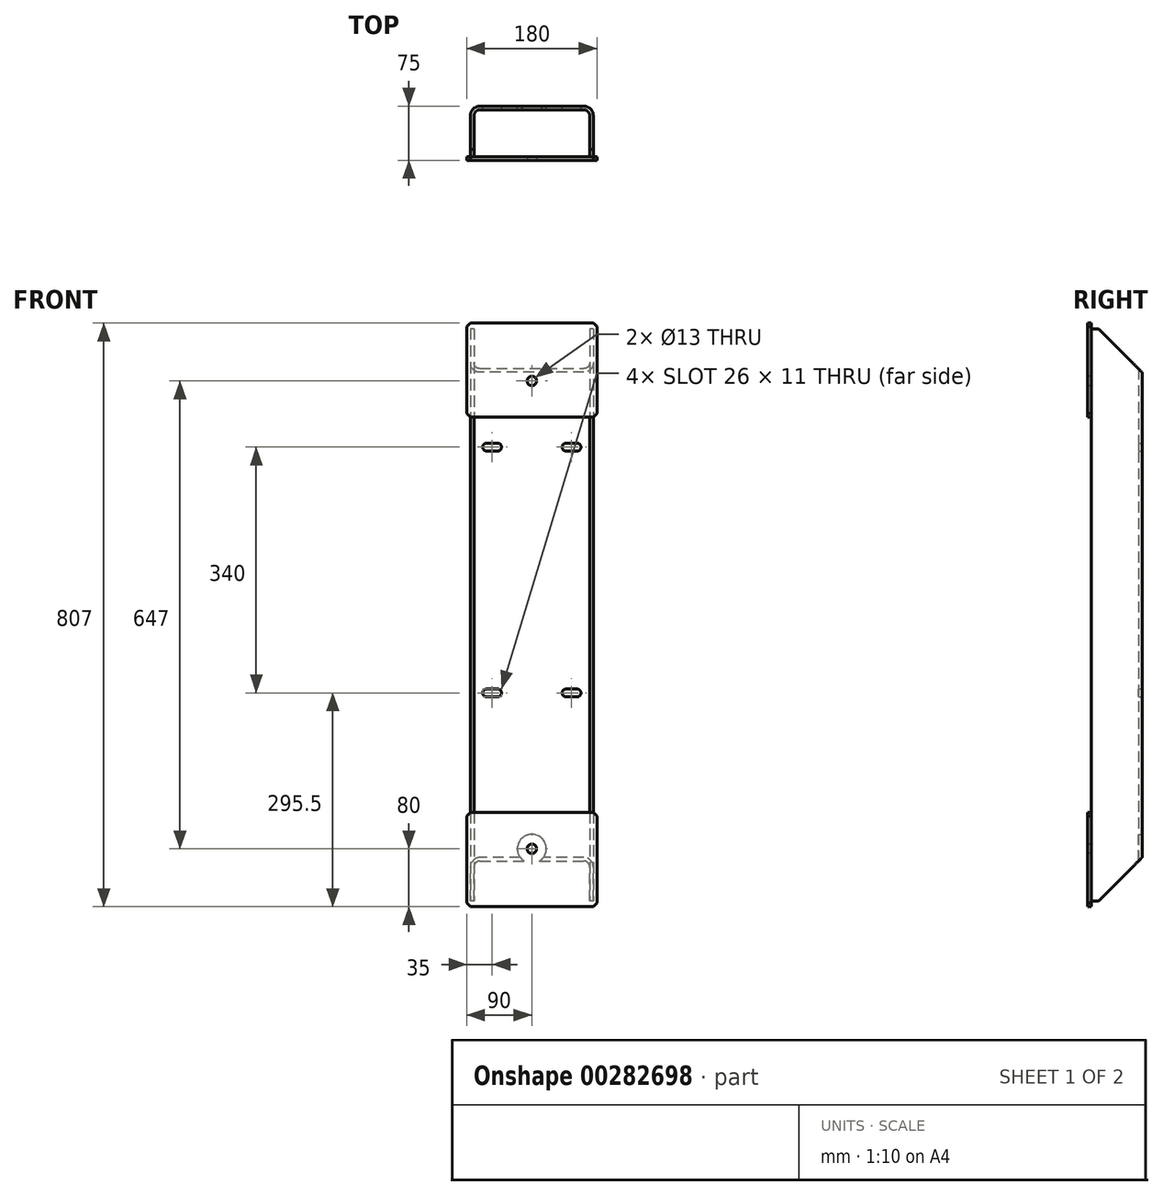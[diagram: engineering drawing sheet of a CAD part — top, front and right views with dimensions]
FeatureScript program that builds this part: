
annotation { "Feature Type Name" : "Feature", "Feature Type Description" : "" }
export const myFeature = defineFeature(function(context is Context, id is Id, definition is map)
    precondition{}
    {
        {
            var Q0;
            Q0=qCreatedBy(makeId("Top.planeOp"),FACE);
            var sketch = newSketch(context, id + "F0", { "sketchPlane" : qUnion([Q0])});
            skLineSegment(sketch, "E0.bottom", {"start": v(-85, 0) * mm, "end": v(-80, 0) * mm});
            skLineSegment(sketch, "E0.top", {"start": v(-72, 70) * mm, "end": v(72, 70) * mm});
            skLineSegment(sketch, "E0.left", {"start": v(-85, 0) * mm, "end": v(-85, 57) * mm});
            skLineSegment(sketch, "E0.right", {"start": v(85, 0) * mm, "end": v(85, 57) * mm});
            skLineSegment(sketch, "E1.0", {"start": v(-72, 65) * mm, "end": v(72, 65) * mm});
            skLineSegment(sketch, "E1.1", {"start": v(-80, 0) * mm, "end": v(-80, 57) * mm});
            skLineSegment(sketch, "E1.3", {"start": v(80, 0) * mm, "end": v(80, 57) * mm});
            skLineSegment(sketch, "E2.trimOffspring", {"start": v(80, 0) * mm, "end": v(85, 0) * mm});
            skPoint(sketch, "E3.visualSharp", {"position": v(-80, 65) * mm});
            skArc(sketch, "E3.filletArc", {"start": v(-72, 65) * mm, "mid": v(-77.66, 62.66) * mm, "end": v(-80, 57) * mm});
            skPoint(sketch, "E4.visualSharp", {"position": v(80, 65) * mm});
            skArc(sketch, "E4.filletArc", {"start": v(80, 57) * mm, "mid": v(77.66, 62.66) * mm, "end": v(72, 65) * mm});
            skPoint(sketch, "E5.visualSharp", {"position": v(-85, 70) * mm});
            skArc(sketch, "E5.filletArc", {"start": v(-72, 70) * mm, "mid": v(-81.2, 66.2) * mm, "end": v(-85, 57) * mm});
            skPoint(sketch, "E6.visualSharp", {"position": v(85, 70) * mm});
            skArc(sketch, "E6.filletArc", {"start": v(85, 57) * mm, "mid": v(81.2, 66.2) * mm, "end": v(72, 70) * mm});
            skSolve(sketch);
        }
        {
            var Q0;
            Q0=makeQuery(id+"F0.imprint","IMPRINT",FACE,{"disambiguationData":[TD([[makeQuery(id+"F0.imprint","IMPRINT",EDGE,{"derivedFrom":sQuery(id+"F0.wireOp",EDGE,"E0.bottom")}),1.0]])]});
            extrude(context, id + "F1", {"entities" : qUnion([Q0]), "depth" : 791 * mm, "symmetric" : true});
        }
        {
            var Q0;
            Q0=makeQuery(id+"F1.opExtrude","SWEPT_FACE",FACE,{"disambiguationData":[OSD([sQuery(id+"F0.wireOp",EDGE,"E0.top")])]});
            var sketch = newSketch(context, id + "F2", { "sketchPlane" : qUnion([Q0])});
            skLineSegment(sketch, "E7", {"start": v(0, -395.5) * mm, "end": v(0, 395.5) * mm, "construction": true});
            skCircle(sketch, "E8", {"center": v(0, -323.5) * mm, "radius": 20 * mm});
            skLineSegment(sketch, "E9", {"start": v(-72, -108) * mm, "end": v(117.06, -108) * mm, "construction": true});
            skArc(sketch, "E10", {"start": v(-62.5, -102.5) * mm, "mid": v(-68, -108) * mm, "end": v(-62.5, -113.5) * mm});
            skArc(sketch, "E11", {"start": v(-47.5, -113.5) * mm, "mid": v(-42, -108) * mm, "end": v(-47.5, -102.5) * mm});
            skLineSegment(sketch, "E12", {"start": v(-62.5, -113.5) * mm, "end": v(-47.5, -113.5) * mm});
            skLineSegment(sketch, "E13", {"start": v(-62.5, -102.5) * mm, "end": v(-47.5, -102.5) * mm});
            skArc(sketch, "E14.MirrorCS", {"start": v(62.5, -102.5) * mm, "mid": v(68, -108) * mm, "end": v(62.5, -113.5) * mm});
            skLineSegment(sketch, "E15.MirrorCS", {"start": v(62.5, -102.5) * mm, "end": v(47.5, -102.5) * mm});
            skLineSegment(sketch, "E16.MirrorCS", {"start": v(62.5, -113.5) * mm, "end": v(47.5, -113.5) * mm});
            skArc(sketch, "E17.MirrorCS", {"start": v(47.5, -113.5) * mm, "mid": v(42, -108) * mm, "end": v(47.5, -102.5) * mm});
            skLineSegment(sketch, "E18", {"start": v(117.06, 62) * mm, "end": v(-190.67, 62) * mm, "construction": true});
            skArc(sketch, "E19.MirrorCS", {"start": v(62.5, 226.5) * mm, "mid": v(68, 232) * mm, "end": v(62.5, 237.5) * mm});
            skLineSegment(sketch, "E20.MirrorCS", {"start": v(62.5, 237.5) * mm, "end": v(47.5, 237.5) * mm});
            skArc(sketch, "E21.MirrorCS", {"start": v(47.5, 237.5) * mm, "mid": v(42, 232) * mm, "end": v(47.5, 226.5) * mm});
            skLineSegment(sketch, "E22.MirrorCS", {"start": v(62.5, 226.5) * mm, "end": v(47.5, 226.5) * mm});
            skLineSegment(sketch, "E23.MirrorCS", {"start": v(-62.5, 237.5) * mm, "end": v(-47.5, 237.5) * mm});
            skLineSegment(sketch, "E24.MirrorCS", {"start": v(-62.5, 226.5) * mm, "end": v(-47.5, 226.5) * mm});
            skArc(sketch, "E25.MirrorCS", {"start": v(-62.5, 226.5) * mm, "mid": v(-68, 232) * mm, "end": v(-62.5, 237.5) * mm});
            skArc(sketch, "E26.MirrorCS", {"start": v(-47.5, 237.5) * mm, "mid": v(-42, 232) * mm, "end": v(-47.5, 226.5) * mm});
            skLineSegment(sketch, "E27.MirrorCS", {"start": v(-72, 232) * mm, "end": v(117.06, 232) * mm, "construction": true});
            skCircle(sketch, "E28.MirrorC", {"center": v(0, 323.5) * mm, "radius": 20 * mm});
            skSolve(sketch);
        }
        {
            var Q0;
            Q0=makeQuery(id+"F2.imprint","IMPRINT",FACE,{"disambiguationData":[TD([[makeQuery(id+"F2.imprint","IMPRINT",EDGE,{"derivedFrom":sQuery(id+"F2.wireOp",EDGE,"E8")}),1.0]])]});
            var Q1;
            Q1=makeQuery(id+"F2.imprint","IMPRINT",FACE,{"disambiguationData":[TD([[makeQuery(id+"F2.imprint","IMPRINT",EDGE,{"derivedFrom":sQuery(id+"F2.wireOp",EDGE,"E11")}),1.0]])]});
            var Q2;
            Q2=makeQuery(id+"F2.imprint","IMPRINT",FACE,{"disambiguationData":[TD([[makeQuery(id+"F2.imprint","IMPRINT",EDGE,{"derivedFrom":sQuery(id+"F2.wireOp",EDGE,"E28.MirrorC")}),-1.0]])]});
            var Q3;
            {var subQ1=sQuery(id+"F2.wireOp",EDGE,"E23.MirrorCS");Q3=makeQuery(id+"F2.imprint","IMPRINT",FACE,{"disambiguationData":[TD([[makeQuery(id+"F2.imprint","IMPRINT",EDGE,{"derivedFrom":subQ1}),-1.0]])]});}
            var Q4;
            {var subQ0=sQuery(id+"F2.wireOp",EDGE,"E20.MirrorCS");Q4=makeQuery(id+"F2.imprint","IMPRINT",FACE,{"disambiguationData":[TD([[makeQuery(id+"F2.imprint","IMPRINT",EDGE,{"derivedFrom":subQ0}),1.0]])]});}
            var Q5;
            {var subQ1=sQuery(id+"F2.wireOp",EDGE,"E15.MirrorCS");Q5=makeQuery(id+"F2.imprint","IMPRINT",FACE,{"disambiguationData":[TD([[makeQuery(id+"F2.imprint","IMPRINT",EDGE,{"derivedFrom":subQ1}),1.0]])]});}
            extrude(context, id + "F3", {"entities" : qUnion([Q0, Q1, Q2, Q3, Q4, Q5]), "operationType" : NewBodyOperationType.REMOVE, "endBound" : BoundingType.THROUGH_ALL, "oppositeDirection" : true, "depth" : 25 * mm});
        }
        {
            var Q0;
            Q0=makeQuery(id+"F1.opExtrude","SWEPT_FACE",FACE,{"disambiguationData":[OSD([sQuery(id+"F0.wireOp",EDGE,"E0.bottom")])]});
            var sketch = newSketch(context, id + "F4", { "sketchPlane" : qUnion([Q0])});
            skLineSegment(sketch, "E29.bottom", {"start": v(-90, -403.5) * mm, "end": v(90, -403.5) * mm});
            skLineSegment(sketch, "E29.top", {"start": v(-90, -273.5) * mm, "end": v(90, -273.5) * mm});
            skLineSegment(sketch, "E29.left", {"start": v(-90, -403.5) * mm, "end": v(-90, -273.5) * mm});
            skLineSegment(sketch, "E29.right", {"start": v(90, -403.5) * mm, "end": v(90, -273.5) * mm});
            skSolve(sketch);
        }
        {
            var Q0;
            Q0=makeQuery(id+"F4.imprint","IMPRINT",FACE,{"disambiguationData":[TD([[makeQuery(id+"F4.imprint","IMPRINT",EDGE,{"derivedFrom":sQuery(id+"F4.wireOp",EDGE,"E29.bottom")}),1.0]])]});
            var Q1;
            {var subQ1=sQuery(id+"F0.wireOp",EDGE,"E0.bottom");var subQ6=makeQuery(id+"F1.opExtrude","CAP_EDGE",EDGE,{"disambiguationData":[OSD([subQ1])],"isStart":true});Q1=makeQuery(id+"F4.imprint","IMPRINT",FACE,{"disambiguationData":[TD([[makeQuery(id+"F4.imprint","IMPRINT",EDGE,{"derivedFrom":subQ6}),1.0]])]});}
            extrude(context, id + "F5", {"entities" : qUnion([Q0, Q1]), "depth" : 5 * mm});
        }
        {
            var Q0;
            Q0=makeQuery(id+"F5.opExtrude","CAP_FACE",FACE,{"disambiguationData":[OSD([sQuery(id+"F4.wireOp",EDGE,"E29.bottom"),sQuery(id+"F4.wireOp",EDGE,"E29.top"),sQuery(id+"F4.wireOp",EDGE,"E29.left"),sQuery(id+"F4.wireOp",EDGE,"E29.right")])],"isStart":false});
            var sketch = newSketch(context, id + "F6", { "sketchPlane" : qUnion([Q0])});
            skCircle(sketch, "E30.0", {"center": v(0, -323.5) * mm, "radius": 20 * mm});
            skCircle(sketch, "E31", {"center": v(0, -323.5) * mm, "radius": 6.5 * mm});
            skSolve(sketch);
        }
        {
            var Q0;
            Q0=makeQuery(id+"F6.imprint","IMPRINT",FACE,{"disambiguationData":[TD([[makeQuery(id+"F6.imprint","IMPRINT",EDGE,{"derivedFrom":sQuery(id+"F6.wireOp",EDGE,"E31")}),1.0]])]});
            extrude(context, id + "F7", {"entities" : qUnion([Q0]), "operationType" : NewBodyOperationType.REMOVE, "endBound" : BoundingType.THROUGH_ALL, "oppositeDirection" : true, "depth" : 25 * mm});
        }
        {
            var Q0;
            Q0=makeQuery(id+"F5.opExtrude","SWEPT_EDGE",EDGE,{"disambiguationData":[OSD([sQuery(id+"F4.wireOp",EDGE,"E29.top"),sQuery(id+"F4.wireOp",EDGE,"E29.left")])]});
            var Q1;
            Q1=makeQuery(id+"F5.opExtrude","SWEPT_EDGE",EDGE,{"disambiguationData":[OSD([sQuery(id+"F4.wireOp",EDGE,"E29.top"),sQuery(id+"F4.wireOp",EDGE,"E29.right")])]});
            var Q2;
            Q2=makeQuery(id+"F5.opExtrude","SWEPT_EDGE",EDGE,{"disambiguationData":[OSD([sQuery(id+"F4.wireOp",EDGE,"E29.bottom"),sQuery(id+"F4.wireOp",EDGE,"E29.left")])]});
            var Q3;
            Q3=makeQuery(id+"F5.opExtrude","SWEPT_EDGE",EDGE,{"disambiguationData":[OSD([sQuery(id+"F4.wireOp",EDGE,"E29.bottom"),sQuery(id+"F4.wireOp",EDGE,"E29.right")])]});
            chamfer(context, id + "F8", {"entities" : qUnion([Q0, Q1, Q2, Q3]), "width" : 5 * mm, "tangentPropagation" : true});
        }
        {
            var Q0;
            Q0=makeQuery(id+"F5.opExtrude","SWEPT_BODY",BODY,{"disambiguationData":[OSD([sQuery(id+"F4.wireOp",EDGE,"E29.bottom"),sQuery(id+"F4.wireOp",EDGE,"E29.top"),sQuery(id+"F4.wireOp",EDGE,"E29.left"),sQuery(id+"F4.wireOp",EDGE,"E29.right")])]});
            var Q1;
            Q1=qCreatedBy(makeId("Top.planeOp"),FACE);
            mirror(context, id + "F9", {"operationType" : NewBodyOperationType.ADD, "entities" : qUnion([Q0]), "mirrorPlane" : qUnion([Q1])});
        }
        {
            var Q0;
            Q0=makeQuery(id+"F1.opExtrude","SWEPT_FACE",FACE,{"disambiguationData":[OSD([sQuery(id+"F0.wireOp",EDGE,"E0.left")])]});
            var sketch = newSketch(context, id + "F10", { "sketchPlane" : qUnion([Q0])});
            skLineSegment(sketch, "E32.0", {"start": v(-10, -395.5) * mm, "end": v(-70, -395.5) * mm});
            skLineSegment(sketch, "E33.0", {"start": v(-70, -335.5) * mm, "end": v(-70, -395.5) * mm});
            skPoint(sketch, "E34.orphan", {"position": v(-57, -395.5) * mm});
            skLineSegment(sketch, "E35", {"start": v(-10, -395.5) * mm, "end": v(-70, -335.5) * mm});
            skPoint(sketch, "E36.orphan", {"position": v(0, -395.5) * mm});
            skPoint(sketch, "E37.orphan", {"position": v(-70, 395.5) * mm});
            skLineSegment(sketch, "E38.MirrorCS", {"start": v(-70, 335.5) * mm, "end": v(-70, 395.5) * mm});
            skLineSegment(sketch, "E39.MirrorCS", {"start": v(-10, 395.5) * mm, "end": v(-70, 335.5) * mm});
            skPoint(sketch, "E40.MirrorP", {"position": v(-57, 395.5) * mm});
            skLineSegment(sketch, "E41.MirrorCS", {"start": v(-10, 395.5) * mm, "end": v(-70, 395.5) * mm});
            skPoint(sketch, "E42.MirrorP", {"position": v(0, 395.5) * mm});
            skSolve(sketch);
        }
        {
            var Q0;
            {var subQ3=sQuery(id+"F10.wireOp",EDGE,"E33.0");Q0=makeQuery(id+"F10.imprint","IMPRINT",FACE,{"disambiguationData":[TD([[makeQuery(id+"F10.imprint","IMPRINT",EDGE,{"derivedFrom":subQ3}),1.0]])]});}
            var Q1;
            {var subQ0=sQuery(id+"F10.wireOp",EDGE,"E32.0");var subQ1=sQuery(id+"F0.wireOp",EDGE,"E0.left");var subQ2=makeQuery(id+"F1.opExtrude","SWEPT_EDGE",EDGE,{"disambiguationData":[OSD([subQ1,sQuery(id+"F0.wireOp",EDGE,"E5.filletArc")])]});var subQ3=makeQuery(id+"F10.imprint","INTERSECT",VERTEX,{"derivedFrom":[subQ2,subQ0]});Q1=makeQuery(id+"F10.imprint","IMPRINT",FACE,{"disambiguationData":[TD([[makeQuery(id+"F10.imprint","IMPRINT",EDGE,{"disambiguationData":[TD([[subQ3,1.0]])],"derivedFrom":subQ0}),-1.0]])]});}
            var Q2;
            {var subQ0=sQuery(id+"F10.wireOp",EDGE,"E38.MirrorCS");Q2=makeQuery(id+"F10.imprint","IMPRINT",FACE,{"disambiguationData":[TD([[makeQuery(id+"F10.imprint","IMPRINT",EDGE,{"derivedFrom":subQ0}),-1.0]])]});}
            var Q3;
            {var subQ0=sQuery(id+"F10.wireOp",EDGE,"E41.MirrorCS");var subQ1=sQuery(id+"F10.wireOp",EDGE,"E39.MirrorCS");var subQ2=sQuery(id+"F0.wireOp",EDGE,"E0.left");var subQ3=makeQuery(id+"F10.imprint","INTERSECT",VERTEX,{"derivedFrom":[makeQuery(id+"F1.opExtrude","CAP_EDGE",EDGE,{"disambiguationData":[OSD([subQ2])],"isStart":false}),subQ1,subQ0]});Q3=makeQuery(id+"F10.imprint","IMPRINT",FACE,{"disambiguationData":[TD([[makeQuery(id+"F10.imprint","IMPRINT",EDGE,{"disambiguationData":[TD([[subQ3,-1.0]])],"derivedFrom":subQ1}),-1.0]])]});}
            extrude(context, id + "F11", {"entities" : qUnion([Q0, Q1, Q2, Q3]), "operationType" : NewBodyOperationType.REMOVE, "endBound" : BoundingType.THROUGH_ALL, "oppositeDirection" : true, "depth" : 25 * mm});
        }
    });
